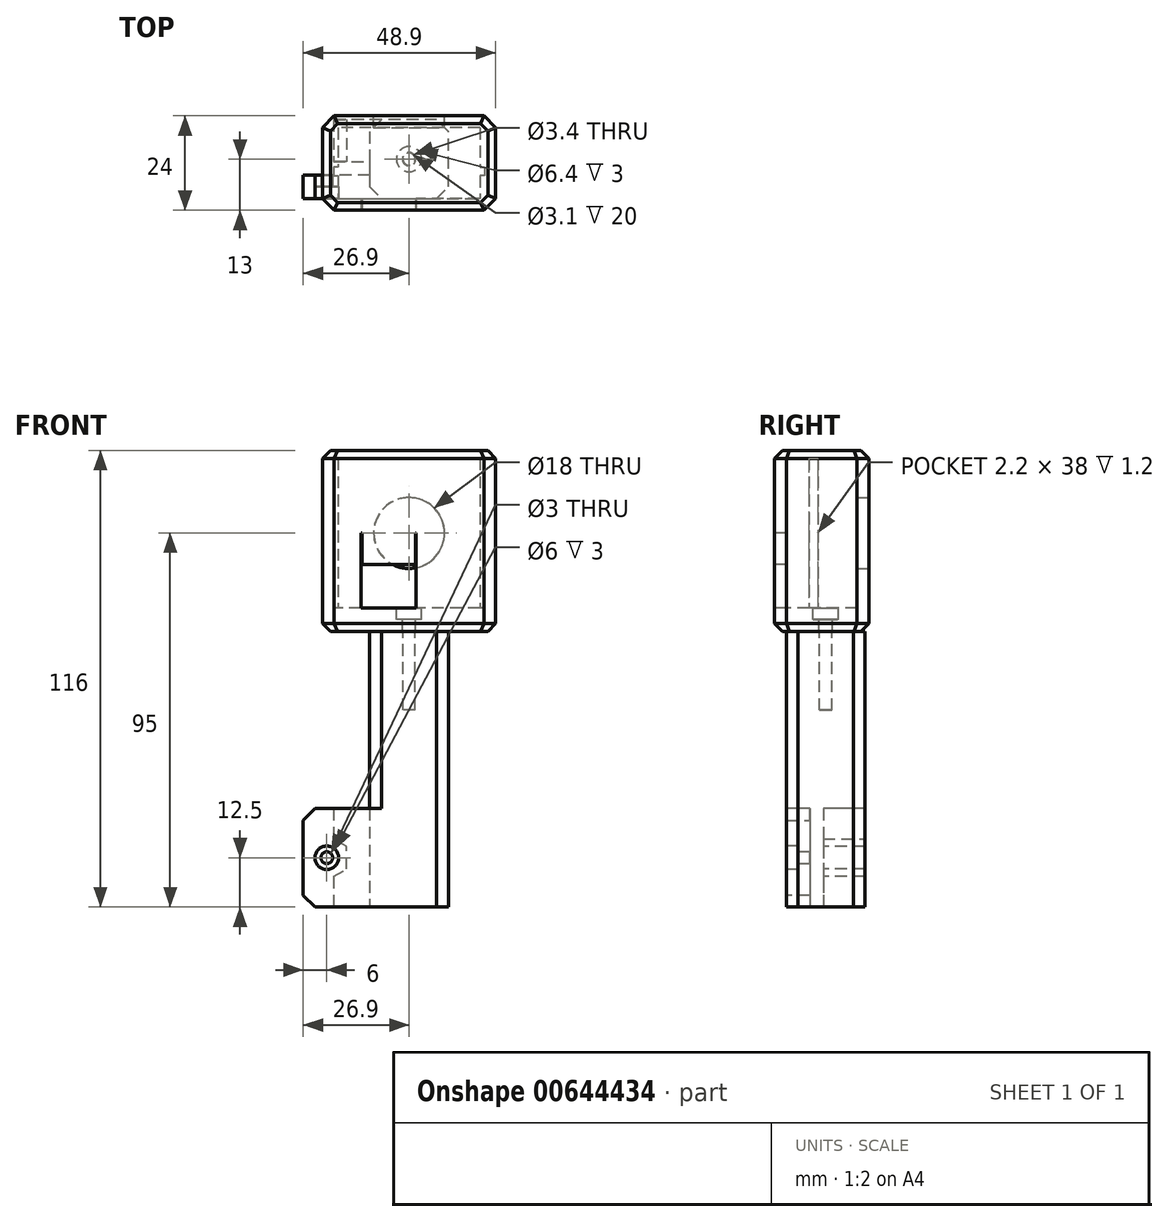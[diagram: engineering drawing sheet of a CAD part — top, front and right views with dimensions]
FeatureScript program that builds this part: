
annotation { "Feature Type Name" : "Feature", "Feature Type Description" : "" }
export const myFeature = defineFeature(function(context is Context, id is Id, definition is map)
    precondition{}
    {
        {
            var Q0;
            Q0=qCreatedBy(makeId("Top.planeOp"),FACE);
            var sketch = newSketch(context, id + "F0", { "sketchPlane" : qUnion([Q0])});
            skLineSegment(sketch, "E0", {"start": v(1.7, 14) * mm, "end": v(1.7, 3.4) * mm});
            skLineSegment(sketch, "E1", {"start": v(1.7, 3.4) * mm, "end": v(10.9, 3.4) * mm});
            skLineSegment(sketch, "E2", {"start": v(10.9, 3.4) * mm, "end": v(10.9, 0) * mm});
            skLineSegment(sketch, "E3", {"start": v(10.9, 0) * mm, "end": v(-6, 0) * mm});
            skLineSegment(sketch, "E4", {"start": v(-6, 0) * mm, "end": v(-6, -6) * mm});
            skLineSegment(sketch, "E5", {"start": v(-6, -6) * mm, "end": v(30.9, -6) * mm});
            skLineSegment(sketch, "E6", {"start": v(30.9, -6) * mm, "end": v(30.9, 14) * mm});
            skLineSegment(sketch, "E7", {"start": v(30.9, 14) * mm, "end": v(1.7, 14) * mm});
            skPoint(sketch, "E8", {"position": v(0, -6) * mm});
            skSolve(sketch);
        }
        {
            var Q0;
            Q0 = qSketchRegion(id + "F0", true);
            extrude(context, id + "F1", {"entities" : qUnion([Q0]), "endBound" : BoundingType.SYMMETRIC, "depth" : 25 * mm, "offsetDistance" : 25 * mm});
        }
        {
            var Q0;
            Q0=makeQuery(id+"F1.opExtrude","SWEPT_FACE",FACE,{"disambiguationData":[OSD([sQuery(id+"F0.wireOp",EDGE,"E5")])]});
            var sketch = newSketch(context, id + "F2", { "sketchPlane" : qUnion([Q0])});
            skCircle(sketch, "E9", {"center": v(0, 0) * mm, "radius": 1.5 * mm});
            skSolve(sketch);
        }
        {
            var Q0;
            Q0 = qSketchRegion(id + "F2", true);
            var Q1;
            Q1=makeQuery(id+"F1.opExtrude","SWEPT_FACE",FACE,{"disambiguationData":[OSD([sQuery(id+"F0.wireOp",EDGE,"E3")])]});
            extrude(context, id + "F3", {"entities" : qUnion([Q0]), "operationType" : NewBodyOperationType.REMOVE, "endBound" : BoundingType.UP_TO_SURFACE, "oppositeDirection" : true, "depth" : 25 * mm, "endBoundEntityFace" : qUnion([Q1]), "offsetDistance" : 25 * mm});
        }
        {
            var Q0;
            Q0=makeQuery(id+"F1.opExtrude","SWEPT_FACE",FACE,{"disambiguationData":[OSD([sQuery(id+"F0.wireOp",EDGE,"E5")])]});
            var sketch = newSketch(context, id + "F4", { "sketchPlane" : qUnion([Q0])});
            skCircle(sketch, "E10", {"center": v(0, 0) * mm, "radius": 3 * mm});
            skSolve(sketch);
        }
        {
            var Q0;
            Q0 = qSketchRegion(id + "F4", true);
            extrude(context, id + "F5", {"entities" : qUnion([Q0]), "operationType" : NewBodyOperationType.REMOVE, "oppositeDirection" : true, "depth" : 3 * mm, "offsetDistance" : 25 * mm});
        }
        {
            var Q0;
            Q0=makeQuery(id+"F1.opExtrude","SWEPT_FACE",FACE,{"disambiguationData":[OSD([sQuery(id+"F0.wireOp",EDGE,"E1")])]});
            var sketch = newSketch(context, id + "F6", { "sketchPlane" : qUnion([Q0])});
            skCircle(sketch, "E11.cCircle", {"center": v(0, 0) * mm, "radius": 5 * mm, "construction": true});
            skLineSegment(sketch, "E11.0", {"start": v(5, 2.89) * mm, "end": v(5, -2.89) * mm});
            skLineSegment(sketch, "E11.1", {"start": v(5, -2.89) * mm, "end": v(0, -5.77) * mm});
            skLineSegment(sketch, "E11.2", {"start": v(0, -5.77) * mm, "end": v(-5, -2.89) * mm});
            skLineSegment(sketch, "E11.3", {"start": v(-5, -2.89) * mm, "end": v(-5, 2.89) * mm});
            skLineSegment(sketch, "E11.4", {"start": v(-5, 2.89) * mm, "end": v(0, 5.77) * mm});
            skLineSegment(sketch, "E11.5", {"start": v(0, 5.77) * mm, "end": v(5, 2.89) * mm});
            skPoint(sketch, "E11.0.midPoint", {"position": v(5, 0) * mm});
            skSolve(sketch);
        }
        {
            var Q0;
            Q0 = qSketchRegion(id + "F6", true);
            var Q1;
            Q1=makeQuery(id+"F1.opExtrude","SWEPT_FACE",FACE,{"disambiguationData":[OSD([sQuery(id+"F0.wireOp",EDGE,"E7")])]});
            extrude(context, id + "F7", {"entities" : qUnion([Q0]), "operationType" : NewBodyOperationType.REMOVE, "endBound" : BoundingType.UP_TO_SURFACE, "oppositeDirection" : true, "depth" : 25 * mm, "endBoundEntityFace" : qUnion([Q1]), "offsetDistance" : 25 * mm});
        }
        {
            var Q0;
            Q0=makeQuery(id+"F1.opExtrude","CAP_FACE",FACE,{"disambiguationData":[OSD([sQuery(id+"F0.wireOp",EDGE,"E0"),sQuery(id+"F0.wireOp",EDGE,"E1"),sQuery(id+"F0.wireOp",EDGE,"E2"),sQuery(id+"F0.wireOp",EDGE,"E3"),sQuery(id+"F0.wireOp",EDGE,"E4"),sQuery(id+"F0.wireOp",EDGE,"E5"),sQuery(id+"F0.wireOp",EDGE,"E6"),sQuery(id+"F0.wireOp",EDGE,"E7")])],"isStart":false});
            var sketch = newSketch(context, id + "F8", { "sketchPlane" : qUnion([Q0])});
            skLineSegment(sketch, "E12.bottom", {"start": v(30.9, 14) * mm, "end": v(10.9, 14) * mm});
            skLineSegment(sketch, "E12.top", {"start": v(30.9, -6) * mm, "end": v(10.9, -6) * mm});
            skLineSegment(sketch, "E12.left", {"start": v(30.9, 14) * mm, "end": v(30.9, -6) * mm});
            skLineSegment(sketch, "E12.right", {"start": v(10.9, 14) * mm, "end": v(10.9, -6) * mm});
            skSolve(sketch);
        }
        {
            var Q0;
            Q0 = qSketchRegion(id + "F8", true);
            extrude(context, id + "F9", {"entities" : qUnion([Q0]), "operationType" : NewBodyOperationType.ADD, "depth" : 45 * mm, "offsetDistance" : 25 * mm});
        }
        {
            var Q0;
            Q0=makeQuery(id+"F9.opExtrude","CAP_FACE",FACE,{"disambiguationData":[OSD([sQuery(id+"F8.wireOp",EDGE,"E12.bottom"),sQuery(id+"F8.wireOp",EDGE,"E12.top"),sQuery(id+"F8.wireOp",EDGE,"E12.left"),sQuery(id+"F8.wireOp",EDGE,"E12.right")])],"isStart":false});
            var sketch = newSketch(context, id + "F10", { "sketchPlane" : qUnion([Q0])});
            skPoint(sketch, "E13", {"position": v(20.9, 4) * mm});
            skPoint(sketch, "E13.positionSnap0", {"position": v(20.9, 14) * mm});
            skPoint(sketch, "E13.positionSnap1", {"position": v(10.9, 4) * mm});
            skCircle(sketch, "E14", {"center": v(20.9, 4) * mm, "radius": 1.55 * mm});
            skSolve(sketch);
        }
        {
            var Q0;
            Q0 = qSketchRegion(id + "F10", true);
            extrude(context, id + "F11", {"entities" : qUnion([Q0]), "operationType" : NewBodyOperationType.REMOVE, "oppositeDirection" : true, "depth" : 20 * mm, "offsetDistance" : 25 * mm});
        }
        {
            var Q0;
            Q0=makeQuery(id+"F9.opExtrude","SWEPT_EDGE",EDGE,{"disambiguationData":[OSD([sQuery(id+"F0.wireOp",EDGE,"E7"),sQuery(id+"F8.wireOp",EDGE,"E12.bottom"),sQuery(id+"F8.wireOp",EDGE,"E12.right")])]});
            var Q1;
            Q1=makeQuery(id+"F9.opExtrude","SWEPT_EDGE",EDGE,{"disambiguationData":[OSD([sQuery(id+"F0.wireOp",EDGE,"E5"),sQuery(id+"F8.wireOp",EDGE,"E12.top"),sQuery(id+"F8.wireOp",EDGE,"E12.right")])]});
            var Q2;
            Q2=makeQuery(id+"F9.boolean.opBoolean","MERGE",EDGE,{"derivedFrom":[makeQuery(id+"F1.opExtrude","SWEPT_EDGE",EDGE,{"disambiguationData":[OSD([sQuery(id+"F0.wireOp",EDGE,"E5"),sQuery(id+"F0.wireOp",EDGE,"E6")])]}),makeQuery(id+"F9.opExtrude","SWEPT_EDGE",EDGE,{"disambiguationData":[OSD([sQuery(id+"F8.wireOp",EDGE,"E12.top"),sQuery(id+"F8.wireOp",EDGE,"E12.left")])]})]});
            var Q3;
            Q3=makeQuery(id+"F9.boolean.opBoolean","MERGE",EDGE,{"derivedFrom":[makeQuery(id+"F1.opExtrude","SWEPT_EDGE",EDGE,{"disambiguationData":[OSD([sQuery(id+"F0.wireOp",EDGE,"E6"),sQuery(id+"F0.wireOp",EDGE,"E7")])]}),makeQuery(id+"F9.opExtrude","SWEPT_EDGE",EDGE,{"disambiguationData":[OSD([sQuery(id+"F8.wireOp",EDGE,"E12.bottom"),sQuery(id+"F8.wireOp",EDGE,"E12.left")])]})]});
            chamfer(context, id + "F12", {"entities" : qUnion([Q0, Q1, Q2, Q3]), "width" : 3 * mm, "tangentPropagation" : true});
        }
        {
            var Q0;
            Q0=makeQuery(id+"F9.opExtrude","CAP_FACE",FACE,{"disambiguationData":[OSD([sQuery(id+"F8.wireOp",EDGE,"E12.bottom"),sQuery(id+"F8.wireOp",EDGE,"E12.top"),sQuery(id+"F8.wireOp",EDGE,"E12.left"),sQuery(id+"F8.wireOp",EDGE,"E12.right")])],"isStart":false});
            var sketch = newSketch(context, id + "F13", { "sketchPlane" : qUnion([Q0])});
            skLineSegment(sketch, "E15.bottom", {"start": v(-1.1, 15) * mm, "end": v(42.9, 15) * mm});
            skLineSegment(sketch, "E15.top", {"start": v(-1.1, -9) * mm, "end": v(42.9, -9) * mm});
            skLineSegment(sketch, "E15.left", {"start": v(-1.1, 15) * mm, "end": v(-1.1, -9) * mm});
            skLineSegment(sketch, "E15.right", {"start": v(42.9, 15) * mm, "end": v(42.9, -9) * mm});
            skPoint(sketch, "E16", {"position": v(20.9, 4) * mm});
            skPoint(sketch, "E17", {"position": v(20.9, 15) * mm});
            skSolve(sketch);
        }
        {
            var Q0;
            Q0 = qSketchRegion(id + "F13", true);
            extrude(context, id + "F14", {"entities" : qUnion([Q0]), "depth" : 6 * mm, "offsetDistance" : 25 * mm});
        }
        {
            var Q0;
            Q0=makeQuery(id+"F14.opExtrude","CAP_FACE",FACE,{"disambiguationData":[OSD([sQuery(id+"F13.wireOp",EDGE,"E15.bottom"),sQuery(id+"F13.wireOp",EDGE,"E15.top"),sQuery(id+"F13.wireOp",EDGE,"E15.left"),sQuery(id+"F13.wireOp",EDGE,"E15.right")])],"isStart":false});
            var sketch = newSketch(context, id + "F15", { "sketchPlane" : qUnion([Q0])});
            skLineSegment(sketch, "E18", {"start": v(11.9, 15) * mm, "end": v(11.9, 12) * mm});
            skLineSegment(sketch, "E19", {"start": v(11.9, 12) * mm, "end": v(2.9, 12) * mm});
            skLineSegment(sketch, "E20", {"start": v(2.9, 12) * mm, "end": v(2.9, 2) * mm});
            skLineSegment(sketch, "E21", {"start": v(2.9, 2) * mm, "end": v(1.7, 2) * mm});
            skLineSegment(sketch, "E22", {"start": v(1.7, 2) * mm, "end": v(1.7, -0.2) * mm});
            skLineSegment(sketch, "E23", {"start": v(1.7, -0.2) * mm, "end": v(2.9, -0.2) * mm});
            skLineSegment(sketch, "E24", {"start": v(2.9, -0.2) * mm, "end": v(2.9, -6) * mm});
            skLineSegment(sketch, "E25", {"start": v(2.9, -6) * mm, "end": v(8.7, -6) * mm});
            skLineSegment(sketch, "E26", {"start": v(8.7, -6) * mm, "end": v(8.7, -9) * mm});
            skLineSegment(sketch, "E27", {"start": v(8.7, -9) * mm, "end": v(-1.1, -9) * mm});
            skLineSegment(sketch, "E28", {"start": v(-1.1, -9) * mm, "end": v(-1.1, 15) * mm});
            skLineSegment(sketch, "E29", {"start": v(-1.1, 15) * mm, "end": v(11.9, 15) * mm});
            skLineSegment(sketch, "E30", {"start": v(29.9, 15) * mm, "end": v(29.9, 12) * mm});
            skLineSegment(sketch, "E31", {"start": v(29.9, 12) * mm, "end": v(38.9, 12) * mm});
            skLineSegment(sketch, "E32", {"start": v(38.9, 12) * mm, "end": v(38.9, 2) * mm});
            skLineSegment(sketch, "E33", {"start": v(38.9, 2) * mm, "end": v(40.1, 2) * mm});
            skLineSegment(sketch, "E34", {"start": v(40.1, 2) * mm, "end": v(40.1, -0.2) * mm});
            skLineSegment(sketch, "E35", {"start": v(40.1, -0.2) * mm, "end": v(38.9, -0.2) * mm});
            skLineSegment(sketch, "E36", {"start": v(38.9, -0.2) * mm, "end": v(38.9, -6) * mm});
            skLineSegment(sketch, "E37", {"start": v(38.9, -6) * mm, "end": v(22.7, -6) * mm});
            skLineSegment(sketch, "E38", {"start": v(22.7, -6) * mm, "end": v(22.7, -9) * mm});
            skLineSegment(sketch, "E39", {"start": v(22.7, -9) * mm, "end": v(42.9, -9) * mm});
            skLineSegment(sketch, "E40", {"start": v(42.9, -9) * mm, "end": v(42.9, 15) * mm});
            skLineSegment(sketch, "E41", {"start": v(42.9, 15) * mm, "end": v(29.9, 15) * mm});
            skLineSegment(sketch, "E42", {"start": v(1.7, 0.9) * mm, "end": v(40.1, 0.9) * mm, "construction": true});
            skPoint(sketch, "E43", {"position": v(20.9, 0.9) * mm});
            skPoint(sketch, "E44", {"position": v(20.9, -9) * mm});
            skLineSegment(sketch, "E45", {"start": v(11.9, 15) * mm, "end": v(29.9, 15) * mm});
            skPoint(sketch, "E46", {"position": v(20.9, 15) * mm});
            skSolve(sketch);
        }
        {
            var Q0;
            Q0 = qSketchRegion(id + "F15", true);
            extrude(context, id + "F16", {"entities" : qUnion([Q0]), "operationType" : NewBodyOperationType.ADD, "depth" : 19 * mm, "offsetDistance" : 25 * mm});
        }
        {
            var Q0;
            Q0=makeQuery(id+"F16.boolean.opBoolean","MERGE",FACE,{"derivedFrom":[makeQuery(id+"F14.opExtrude","SWEPT_FACE",FACE,{"disambiguationData":[OSD([sQuery(id+"F13.wireOp",EDGE,"E15.bottom")])]}),makeQuery(id+"F16.opExtrude","SWEPT_FACE",FACE,{"disambiguationData":[OSD([sQuery(id+"F15.wireOp",EDGE,"E29")])]}),makeQuery(id+"F16.opExtrude","SWEPT_FACE",FACE,{"disambiguationData":[OSD([sQuery(id+"F15.wireOp",EDGE,"E41")])]})]});
            var sketch = newSketch(context, id + "F17", { "sketchPlane" : qUnion([Q0])});
            skArc(sketch, "E47", {"start": v(-29.9, 82.5) * mm, "mid": v(-20.9, 73.5) * mm, "end": v(-11.9, 82.5) * mm});
            skLineSegment(sketch, "E48", {"start": v(-29.9, 82.5) * mm, "end": v(-29.9, 63.5) * mm});
            skLineSegment(sketch, "E49", {"start": v(-29.9, 63.5) * mm, "end": v(-11.9, 63.5) * mm});
            skLineSegment(sketch, "E50", {"start": v(-11.9, 63.5) * mm, "end": v(-11.9, 82.5) * mm});
            skSolve(sketch);
        }
        {
            var Q0;
            Q0 = qSketchRegion(id + "F17", true);
            var Q1;
            Q1=makeQuery(id+"F16.opExtrude","SWEPT_FACE",FACE,{"disambiguationData":[OSD([sQuery(id+"F15.wireOp",EDGE,"E31")])]});
            extrude(context, id + "F18", {"entities" : qUnion([Q0]), "operationType" : NewBodyOperationType.ADD, "endBound" : BoundingType.UP_TO_SURFACE, "oppositeDirection" : true, "depth" : 25 * mm, "endBoundEntityFace" : qUnion([Q1]), "offsetDistance" : 25 * mm});
        }
        {
            var Q0;
            Q0=makeQuery(id+"F16.boolean.opBoolean","MERGE",EDGE,{"derivedFrom":[makeQuery(id+"F14.opExtrude","SWEPT_EDGE",EDGE,{"disambiguationData":[OSD([sQuery(id+"F13.wireOp",EDGE,"E15.bottom"),sQuery(id+"F13.wireOp",EDGE,"E15.right")])]}),makeQuery(id+"F16.opExtrude","SWEPT_EDGE",EDGE,{"disambiguationData":[OSD([sQuery(id+"F15.wireOp",EDGE,"E40"),sQuery(id+"F15.wireOp",EDGE,"E41")])]})]});
            var Q1;
            Q1=makeQuery(id+"F16.boolean.opBoolean","MERGE",EDGE,{"derivedFrom":[makeQuery(id+"F14.opExtrude","SWEPT_EDGE",EDGE,{"disambiguationData":[OSD([sQuery(id+"F13.wireOp",EDGE,"E15.bottom"),sQuery(id+"F13.wireOp",EDGE,"E15.left")])]}),makeQuery(id+"F16.opExtrude","SWEPT_EDGE",EDGE,{"disambiguationData":[OSD([sQuery(id+"F15.wireOp",EDGE,"E28"),sQuery(id+"F15.wireOp",EDGE,"E29")])]})]});
            var Q2;
            Q2=makeQuery(id+"F16.boolean.opBoolean","MERGE",EDGE,{"derivedFrom":[makeQuery(id+"F14.opExtrude","SWEPT_EDGE",EDGE,{"disambiguationData":[OSD([sQuery(id+"F13.wireOp",EDGE,"E15.top"),sQuery(id+"F13.wireOp",EDGE,"E15.left")])]}),makeQuery(id+"F16.opExtrude","SWEPT_EDGE",EDGE,{"disambiguationData":[OSD([sQuery(id+"F15.wireOp",EDGE,"E27"),sQuery(id+"F15.wireOp",EDGE,"E28")])]})]});
            var Q3;
            Q3=makeQuery(id+"F16.boolean.opBoolean","MERGE",EDGE,{"derivedFrom":[makeQuery(id+"F14.opExtrude","SWEPT_EDGE",EDGE,{"disambiguationData":[OSD([sQuery(id+"F13.wireOp",EDGE,"E15.top"),sQuery(id+"F13.wireOp",EDGE,"E15.right")])]}),makeQuery(id+"F16.opExtrude","SWEPT_EDGE",EDGE,{"disambiguationData":[OSD([sQuery(id+"F15.wireOp",EDGE,"E39"),sQuery(id+"F15.wireOp",EDGE,"E40")])]})]});
            chamfer(context, id + "F19", {"entities" : qUnion([Q0, Q1, Q2, Q3]), "width" : 3 * mm, "tangentPropagation" : true});
        }
        {
            var Q0;
            Q0=makeQuery(id+"F16.opExtrude","CAP_FACE",FACE,{"disambiguationData":[OSD([sQuery(id+"F15.wireOp",EDGE,"E18"),sQuery(id+"F15.wireOp",EDGE,"E19"),sQuery(id+"F15.wireOp",EDGE,"E20"),sQuery(id+"F15.wireOp",EDGE,"E21"),sQuery(id+"F15.wireOp",EDGE,"E22"),sQuery(id+"F15.wireOp",EDGE,"E23"),sQuery(id+"F15.wireOp",EDGE,"E24"),sQuery(id+"F15.wireOp",EDGE,"E25"),sQuery(id+"F15.wireOp",EDGE,"E26"),sQuery(id+"F15.wireOp",EDGE,"E27"),sQuery(id+"F15.wireOp",EDGE,"E28"),sQuery(id+"F15.wireOp",EDGE,"E29")])],"isStart":false});
            var sketch = newSketch(context, id + "F20", { "sketchPlane" : qUnion([Q0])});
            skLineSegment(sketch, "E51", {"start": v(1.9, 15) * mm, "end": v(-1.1, 12) * mm});
            skLineSegment(sketch, "E52", {"start": v(-1.1, 12) * mm, "end": v(-1.1, -6) * mm});
            skLineSegment(sketch, "E53", {"start": v(-1.1, -6) * mm, "end": v(1.9, -9) * mm});
            skLineSegment(sketch, "E54", {"start": v(1.9, -9) * mm, "end": v(8.7, -9) * mm});
            skLineSegment(sketch, "E55", {"start": v(8.7, -9) * mm, "end": v(8.7, -6) * mm});
            skLineSegment(sketch, "E56", {"start": v(8.7, -6) * mm, "end": v(2.9, -6) * mm});
            skLineSegment(sketch, "E57", {"start": v(2.9, -6) * mm, "end": v(2.9, -0.2) * mm});
            skLineSegment(sketch, "E58", {"start": v(2.9, -0.2) * mm, "end": v(1.7, -0.2) * mm});
            skLineSegment(sketch, "E59", {"start": v(1.7, -0.2) * mm, "end": v(1.7, 2) * mm});
            skLineSegment(sketch, "E60", {"start": v(1.7, 2) * mm, "end": v(2.9, 2) * mm});
            skLineSegment(sketch, "E61", {"start": v(2.9, 2) * mm, "end": v(2.9, 12) * mm});
            skLineSegment(sketch, "E62", {"start": v(2.9, 12) * mm, "end": v(11.9, 12) * mm});
            skLineSegment(sketch, "E63", {"start": v(11.9, 12) * mm, "end": v(11.9, 15) * mm});
            skLineSegment(sketch, "E64", {"start": v(11.9, 15) * mm, "end": v(1.9, 15) * mm});
            skLineSegment(sketch, "E65", {"start": v(39.9, 15) * mm, "end": v(42.9, 12) * mm});
            skLineSegment(sketch, "E66", {"start": v(42.9, 12) * mm, "end": v(42.9, -6) * mm});
            skLineSegment(sketch, "E67", {"start": v(42.9, -6) * mm, "end": v(39.9, -9) * mm});
            skLineSegment(sketch, "E68", {"start": v(39.9, -9) * mm, "end": v(22.7, -9) * mm});
            skLineSegment(sketch, "E69", {"start": v(22.7, -9) * mm, "end": v(22.7, -6) * mm});
            skLineSegment(sketch, "E70", {"start": v(22.7, -6) * mm, "end": v(38.9, -6) * mm});
            skLineSegment(sketch, "E71", {"start": v(38.9, -6) * mm, "end": v(38.9, -0.2) * mm});
            skLineSegment(sketch, "E72", {"start": v(38.9, -0.2) * mm, "end": v(40.1, -0.2) * mm});
            skLineSegment(sketch, "E73", {"start": v(40.1, -0.2) * mm, "end": v(40.1, 2) * mm});
            skLineSegment(sketch, "E74", {"start": v(40.1, 2) * mm, "end": v(38.9, 2) * mm});
            skLineSegment(sketch, "E75", {"start": v(38.9, 2) * mm, "end": v(38.9, 12) * mm});
            skLineSegment(sketch, "E76", {"start": v(38.9, 12) * mm, "end": v(29.9, 12) * mm});
            skLineSegment(sketch, "E77", {"start": v(29.9, 12) * mm, "end": v(29.9, 15) * mm});
            skLineSegment(sketch, "E78", {"start": v(29.9, 15) * mm, "end": v(39.9, 15) * mm});
            skSolve(sketch);
        }
        {
            var Q0;
            Q0 = qSketchRegion(id + "F20", true);
            extrude(context, id + "F21", {"entities" : qUnion([Q0]), "depth" : 19 * mm, "offsetDistance" : 25 * mm});
        }
        {
            var Q0;
            Q0=makeQuery(id+"F21.opExtrude","CAP_FACE",FACE,{"disambiguationData":[OSD([sQuery(id+"F20.wireOp",EDGE,"E51"),sQuery(id+"F20.wireOp",EDGE,"E52"),sQuery(id+"F20.wireOp",EDGE,"E53"),sQuery(id+"F20.wireOp",EDGE,"E54"),sQuery(id+"F20.wireOp",EDGE,"E55"),sQuery(id+"F20.wireOp",EDGE,"E56"),sQuery(id+"F20.wireOp",EDGE,"E57"),sQuery(id+"F20.wireOp",EDGE,"E58"),sQuery(id+"F20.wireOp",EDGE,"E59"),sQuery(id+"F20.wireOp",EDGE,"E60"),sQuery(id+"F20.wireOp",EDGE,"E61"),sQuery(id+"F20.wireOp",EDGE,"E62"),sQuery(id+"F20.wireOp",EDGE,"E63"),sQuery(id+"F20.wireOp",EDGE,"E64")])],"isStart":false});
            var sketch = newSketch(context, id + "F22", { "sketchPlane" : qUnion([Q0])});
            skLineSegment(sketch, "E79", {"start": v(1.9, 15) * mm, "end": v(-1.1, 12) * mm});
            skLineSegment(sketch, "E80", {"start": v(-1.1, 12) * mm, "end": v(-1.1, -6) * mm});
            skLineSegment(sketch, "E81", {"start": v(-1.1, -6) * mm, "end": v(1.9, -9) * mm});
            skLineSegment(sketch, "E82", {"start": v(1.9, -9) * mm, "end": v(39.9, -9) * mm});
            skLineSegment(sketch, "E83", {"start": v(39.9, -9) * mm, "end": v(42.9, -6) * mm});
            skLineSegment(sketch, "E84", {"start": v(42.9, -6) * mm, "end": v(42.9, 12) * mm});
            skLineSegment(sketch, "E85", {"start": v(42.9, 12) * mm, "end": v(39.9, 15) * mm});
            skLineSegment(sketch, "E86", {"start": v(39.9, 15) * mm, "end": v(1.9, 15) * mm});
            skSolve(sketch);
        }
        {
            var Q0;
            Q0 = qSketchRegion(id + "F22", true);
            extrude(context, id + "F23", {"entities" : qUnion([Q0]), "operationType" : NewBodyOperationType.ADD, "depth" : 2 * mm, "offsetDistance" : 25 * mm});
        }
        {
            var Q0;
            Q0=makeQuery(id+"F23.boolean.opBoolean","MERGE",FACE,{"derivedFrom":[makeQuery(id+"F21.opExtrude","SWEPT_FACE",FACE,{"disambiguationData":[OSD([sQuery(id+"F20.wireOp",EDGE,"E54")])]}),makeQuery(id+"F21.opExtrude","SWEPT_FACE",FACE,{"disambiguationData":[OSD([sQuery(id+"F20.wireOp",EDGE,"E68")])]}),makeQuery(id+"F23.opExtrude","SWEPT_FACE",FACE,{"disambiguationData":[OSD([sQuery(id+"F22.wireOp",EDGE,"E82")])]})]});
            var sketch = newSketch(context, id + "F24", { "sketchPlane" : qUnion([Q0])});
            skLineSegment(sketch, "E87.bottom", {"start": v(8.7, 101.5) * mm, "end": v(22.7, 101.5) * mm});
            skLineSegment(sketch, "E87.top", {"start": v(8.7, 82.5) * mm, "end": v(22.7, 82.5) * mm});
            skLineSegment(sketch, "E87.left", {"start": v(8.7, 101.5) * mm, "end": v(8.7, 82.5) * mm});
            skLineSegment(sketch, "E87.right", {"start": v(22.7, 101.5) * mm, "end": v(22.7, 82.5) * mm});
            skLineSegment(sketch, "E88.bottom", {"start": v(8.9, 82.5) * mm, "end": v(22.5, 82.5) * mm});
            skLineSegment(sketch, "E88.top", {"start": v(8.9, 74.5) * mm, "end": v(22.5, 74.5) * mm});
            skLineSegment(sketch, "E88.left", {"start": v(8.9, 82.5) * mm, "end": v(8.9, 74.5) * mm});
            skLineSegment(sketch, "E88.right", {"start": v(22.5, 82.5) * mm, "end": v(22.5, 74.5) * mm});
            skSolve(sketch);
        }
        {
            var Q0;
            Q0 = qSketchRegion(id + "F24", true);
            var Q1;
            Q1=makeQuery(id+"F16.opExtrude","SWEPT_FACE",FACE,{"disambiguationData":[OSD([sQuery(id+"F15.wireOp",EDGE,"E25")])]});
            extrude(context, id + "F25", {"entities" : qUnion([Q0]), "operationType" : NewBodyOperationType.ADD, "endBound" : BoundingType.UP_TO_SURFACE, "oppositeDirection" : true, "depth" : 3 * mm, "endBoundEntityFace" : qUnion([Q1]), "offsetDistance" : 25 * mm});
        }
        {
            var Q0;
            Q0=makeQuery(id+"F23.boolean.opBoolean","MERGE",FACE,{"derivedFrom":[makeQuery(id+"F21.opExtrude","SWEPT_FACE",FACE,{"disambiguationData":[OSD([sQuery(id+"F20.wireOp",EDGE,"E64")])]}),makeQuery(id+"F21.opExtrude","SWEPT_FACE",FACE,{"disambiguationData":[OSD([sQuery(id+"F20.wireOp",EDGE,"E78")])]}),makeQuery(id+"F23.opExtrude","SWEPT_FACE",FACE,{"disambiguationData":[OSD([sQuery(id+"F22.wireOp",EDGE,"E86")])]})]});
            var sketch = newSketch(context, id + "F26", { "sketchPlane" : qUnion([Q0])});
            skArc(sketch, "E89", {"start": v(-11.9, 82.5) * mm, "mid": v(-20.9, 91.5) * mm, "end": v(-29.9, 82.5) * mm});
            skLineSegment(sketch, "E90", {"start": v(-29.9, 82.5) * mm, "end": v(-29.9, 101.5) * mm});
            skLineSegment(sketch, "E91", {"start": v(-29.9, 101.5) * mm, "end": v(-11.9, 101.5) * mm});
            skLineSegment(sketch, "E92", {"start": v(-11.9, 101.5) * mm, "end": v(-11.9, 82.5) * mm});
            skSolve(sketch);
        }
        {
            var Q0;
            Q0 = qSketchRegion(id + "F26", true);
            var Q1;
            {var subQ0=sQuery(id+"F15.wireOp",EDGE,"E31");Q1=makeQuery(id+"F18.boolean.opBoolean","MERGE",FACE,{"derivedFrom":[makeQuery(id+"F16.opExtrude","SWEPT_FACE",FACE,{"disambiguationData":[OSD([sQuery(id+"F15.wireOp",EDGE,"E19")])]}),makeQuery(id+"F16.opExtrude","SWEPT_FACE",FACE,{"disambiguationData":[OSD([subQ0])]}),makeQuery(id+"F18.opExtrude","CAP_FACE",FACE,{"disambiguationData":[OSD([subQ0])],"isStart":false})]});}
            extrude(context, id + "F27", {"entities" : qUnion([Q0]), "operationType" : NewBodyOperationType.ADD, "endBound" : BoundingType.UP_TO_SURFACE, "oppositeDirection" : true, "depth" : 25 * mm, "endBoundEntityFace" : qUnion([Q1]), "offsetDistance" : 25 * mm});
        }
        {
            var Q0;
            Q0=makeQuery(id+"F23.opExtrude","CAP_FACE",FACE,{"disambiguationData":[OSD([sQuery(id+"F22.wireOp",EDGE,"E79"),sQuery(id+"F22.wireOp",EDGE,"E80"),sQuery(id+"F22.wireOp",EDGE,"E81"),sQuery(id+"F22.wireOp",EDGE,"E82"),sQuery(id+"F22.wireOp",EDGE,"E83"),sQuery(id+"F22.wireOp",EDGE,"E84"),sQuery(id+"F22.wireOp",EDGE,"E85"),sQuery(id+"F22.wireOp",EDGE,"E86")])],"isStart":false});
            var Q1;
            Q1=makeQuery(id+"F14.opExtrude","CAP_FACE",FACE,{"disambiguationData":[OSD([sQuery(id+"F13.wireOp",EDGE,"E15.bottom"),sQuery(id+"F13.wireOp",EDGE,"E15.top"),sQuery(id+"F13.wireOp",EDGE,"E15.left"),sQuery(id+"F13.wireOp",EDGE,"E15.right")])],"isStart":true});
            chamfer(context, id + "F28", {"entities" : qUnion([Q0, Q1]), "width" : 2 * mm, "tangentPropagation" : true});
        }
        {
            var Q0;
            Q0=makeQuery(id+"F14.opExtrude","CAP_FACE",FACE,{"disambiguationData":[OSD([sQuery(id+"F13.wireOp",EDGE,"E15.bottom"),sQuery(id+"F13.wireOp",EDGE,"E15.top"),sQuery(id+"F13.wireOp",EDGE,"E15.left"),sQuery(id+"F13.wireOp",EDGE,"E15.right")])],"isStart":false});
            var sketch = newSketch(context, id + "F29", { "sketchPlane" : qUnion([Q0])});
            skCircle(sketch, "E93", {"center": v(20.9, 4) * mm, "radius": 1.7 * mm});
            skSolve(sketch);
        }
        {
            var Q0;
            Q0 = qSketchRegion(id + "F29", true);
            var Q1;
            Q1=makeQuery(id+"F14.opExtrude","CAP_FACE",FACE,{"disambiguationData":[OSD([sQuery(id+"F13.wireOp",EDGE,"E15.bottom"),sQuery(id+"F13.wireOp",EDGE,"E15.top"),sQuery(id+"F13.wireOp",EDGE,"E15.left"),sQuery(id+"F13.wireOp",EDGE,"E15.right")])],"isStart":true});
            extrude(context, id + "F30", {"entities" : qUnion([Q0]), "operationType" : NewBodyOperationType.REMOVE, "endBound" : BoundingType.UP_TO_SURFACE, "oppositeDirection" : true, "depth" : 25 * mm, "endBoundEntityFace" : qUnion([Q1]), "offsetDistance" : 25 * mm});
        }
        {
            var Q0;
            Q0=makeQuery(id+"F14.opExtrude","CAP_FACE",FACE,{"disambiguationData":[OSD([sQuery(id+"F13.wireOp",EDGE,"E15.bottom"),sQuery(id+"F13.wireOp",EDGE,"E15.top"),sQuery(id+"F13.wireOp",EDGE,"E15.left"),sQuery(id+"F13.wireOp",EDGE,"E15.right")])],"isStart":false});
            var sketch = newSketch(context, id + "F31", { "sketchPlane" : qUnion([Q0])});
            skCircle(sketch, "E94", {"center": v(20.9, 4) * mm, "radius": 3.2 * mm});
            skSolve(sketch);
        }
        {
            var Q0;
            Q0 = qSketchRegion(id + "F31", true);
            extrude(context, id + "F32", {"entities" : qUnion([Q0]), "operationType" : NewBodyOperationType.REMOVE, "oppositeDirection" : true, "depth" : 3 * mm, "offsetDistance" : 25 * mm});
        }
        {
            var Q0;
            Q0=makeQuery(id+"F1.opExtrude","CAP_EDGE",EDGE,{"disambiguationData":[OSD([sQuery(id+"F0.wireOp",EDGE,"E4")])],"isStart":false});
            var Q1;
            Q1=makeQuery(id+"F1.opExtrude","CAP_EDGE",EDGE,{"disambiguationData":[OSD([sQuery(id+"F0.wireOp",EDGE,"E4")])],"isStart":true});
            chamfer(context, id + "F33", {"entities" : qUnion([Q0, Q1]), "width" : 3 * mm, "tangentPropagation" : true});
        }
    });
